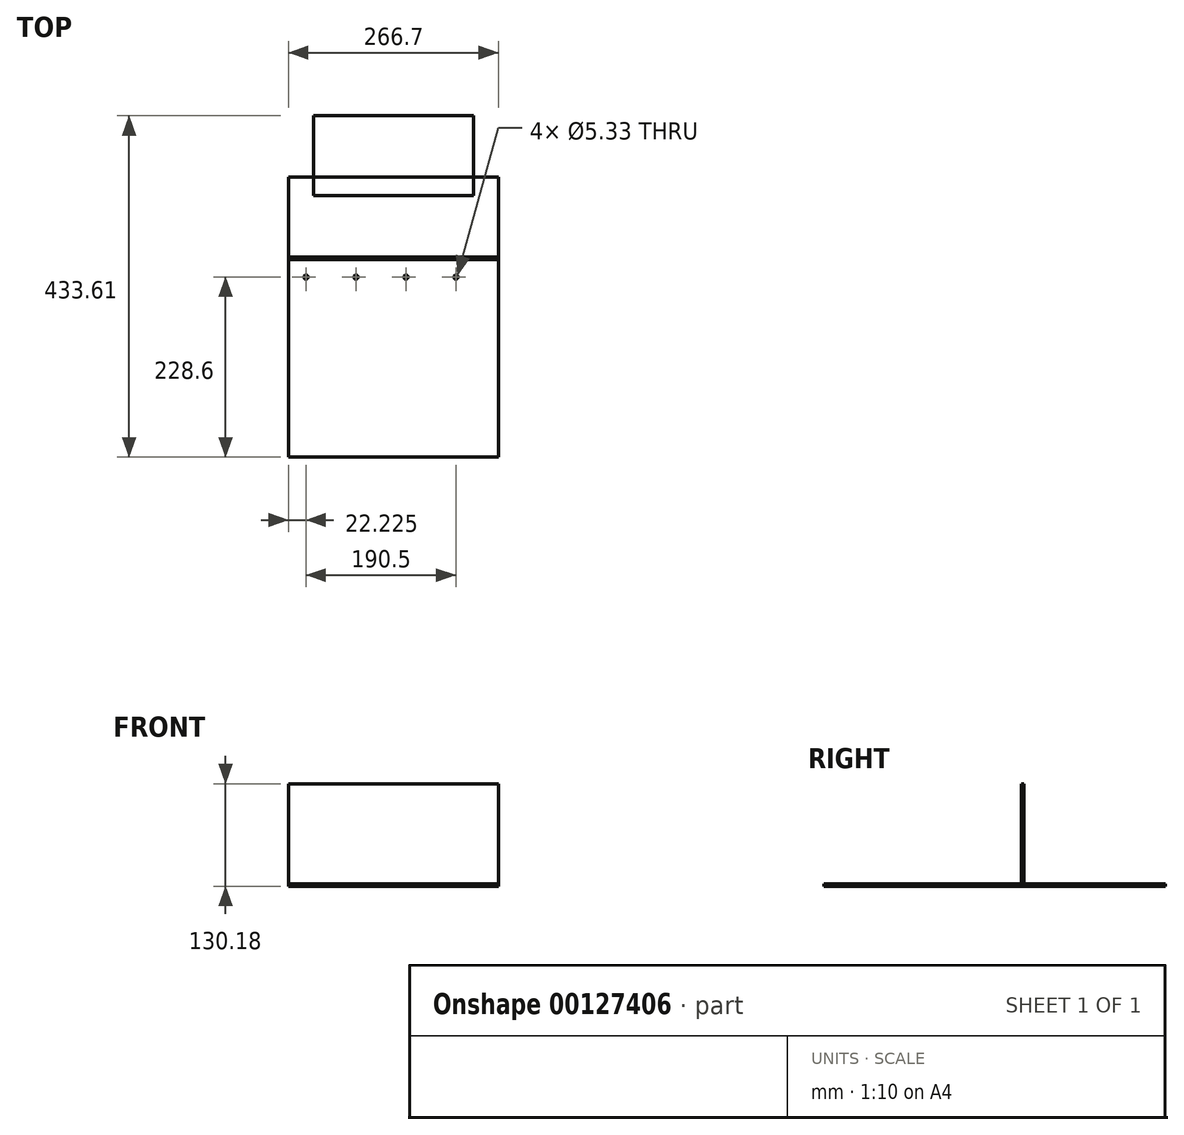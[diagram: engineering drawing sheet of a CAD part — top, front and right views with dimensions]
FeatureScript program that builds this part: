
annotation { "Feature Type Name" : "Feature", "Feature Type Description" : "" }
export const myFeature = defineFeature(function(context is Context, id is Id, definition is map)
    precondition{}
    {
        {
            var Q0;
            Q0=qCreatedBy(makeId("Top.planeOp"),FACE);
            var sketch = newSketch(context, id + "F0", { "sketchPlane" : qUnion([Q0])});
            skLineSegment(sketch, "E0.bottom", {"start": v(-133.35, 177.8) * mm, "end": v(133.35, 177.8) * mm});
            skLineSegment(sketch, "E0.top", {"start": v(-133.35, -177.8) * mm, "end": v(133.35, -177.8) * mm});
            skLineSegment(sketch, "E0.left", {"start": v(-133.35, 177.8) * mm, "end": v(-133.35, -177.8) * mm});
            skLineSegment(sketch, "E0.right", {"start": v(133.35, 177.8) * mm, "end": v(133.35, -177.8) * mm});
            skPoint(sketch, "E0.middle", {"position": v(0, 0) * mm});
            skCircle(sketch, "E1", {"center": v(-111.12, 50.8) * mm, "radius": 2.67 * mm});
            skCircle(sketch, "E2.1.0.0", {"center": v(-47.62, 50.8) * mm, "radius": 2.67 * mm});
            skCircle(sketch, "E2.2.0.0", {"center": v(15.88, 50.8) * mm, "radius": 2.67 * mm});
            skCircle(sketch, "E2.3.0.0", {"center": v(79.38, 50.8) * mm, "radius": 2.67 * mm});
            skLineSegment(sketch, "E2.direction1", {"start": v(-111.12, 50.8) * mm, "end": v(-47.62, 50.8) * mm, "construction": true});
            skLineSegment(sketch, "E3", {"start": v(-47.62, 50.8) * mm, "end": v(15.88, 50.8) * mm, "construction": true});
            skPoint(sketch, "E4", {"position": v(-15.88, 50.8) * mm});
            skPoint(sketch, "E5", {"position": v(0, 50.8) * mm});
            skSolve(sketch);
        }
        {
            var Q0;
            Q0 = qSketchRegion(id + "F0", true);
            extrude(context, id + "F1", {"entities" : qUnion([Q0]), "depth" : 3.17 * mm});
        }
        {
            var Q0;
            Q0=qCreatedBy(makeId("Top.planeOp"),FACE);
            var sketch = newSketch(context, id + "F2", { "sketchPlane" : qUnion([Q0])});
            skLineSegment(sketch, "E6.bottom", {"start": v(-101.6, 255.81) * mm, "end": v(101.6, 255.81) * mm});
            skLineSegment(sketch, "E6.top", {"start": v(-101.6, 154.21) * mm, "end": v(101.6, 154.21) * mm});
            skLineSegment(sketch, "E6.left", {"start": v(-101.6, 255.81) * mm, "end": v(-101.6, 154.21) * mm});
            skLineSegment(sketch, "E6.right", {"start": v(101.6, 255.81) * mm, "end": v(101.6, 154.21) * mm});
            skPoint(sketch, "E6.middle", {"position": v(0, 205.01) * mm});
            skSolve(sketch);
        }
        {
            var Q0;
            Q0 = qSketchRegion(id + "F2", true);
            extrude(context, id + "F3", {"entities" : qUnion([Q0]), "depth" : 3.17 * mm});
        }
        {
            var Q0;
            Q0=qCreatedBy(makeId("Front.planeOp"),FACE);
            cPlane(context, id + "F4", {"entities" : qUnion([Q0]), "cplaneType" : CPlaneType.OFFSET, "offset" : 76.2 * mm, "oppositeDirection" : true, "width" : 152.4 * mm, "height" : 152.4 * mm});
        }
        {
            var Q0;
            Q0=qCreatedBy(id+"F4.planeOp",FACE);
            var sketch = newSketch(context, id + "F5", { "sketchPlane" : qUnion([Q0])});
            skLineSegment(sketch, "E7.bottom", {"start": v(-133.35, 3.18) * mm, "end": v(133.35, 3.18) * mm});
            skLineSegment(sketch, "E7.top", {"start": v(-133.35, 130.18) * mm, "end": v(133.35, 130.18) * mm});
            skLineSegment(sketch, "E7.left", {"start": v(-133.35, 3.17) * mm, "end": v(-133.35, 130.18) * mm});
            skLineSegment(sketch, "E7.right", {"start": v(133.35, 3.17) * mm, "end": v(133.35, 130.18) * mm});
            skPoint(sketch, "E7.middle", {"position": v(0, 66.68) * mm});
            skSolve(sketch);
        }
        {
            var Q0;
            Q0 = qSketchRegion(id + "F5", true);
            extrude(context, id + "F6", {"entities" : qUnion([Q0]), "depth" : 3.17 * mm});
        }
    });
